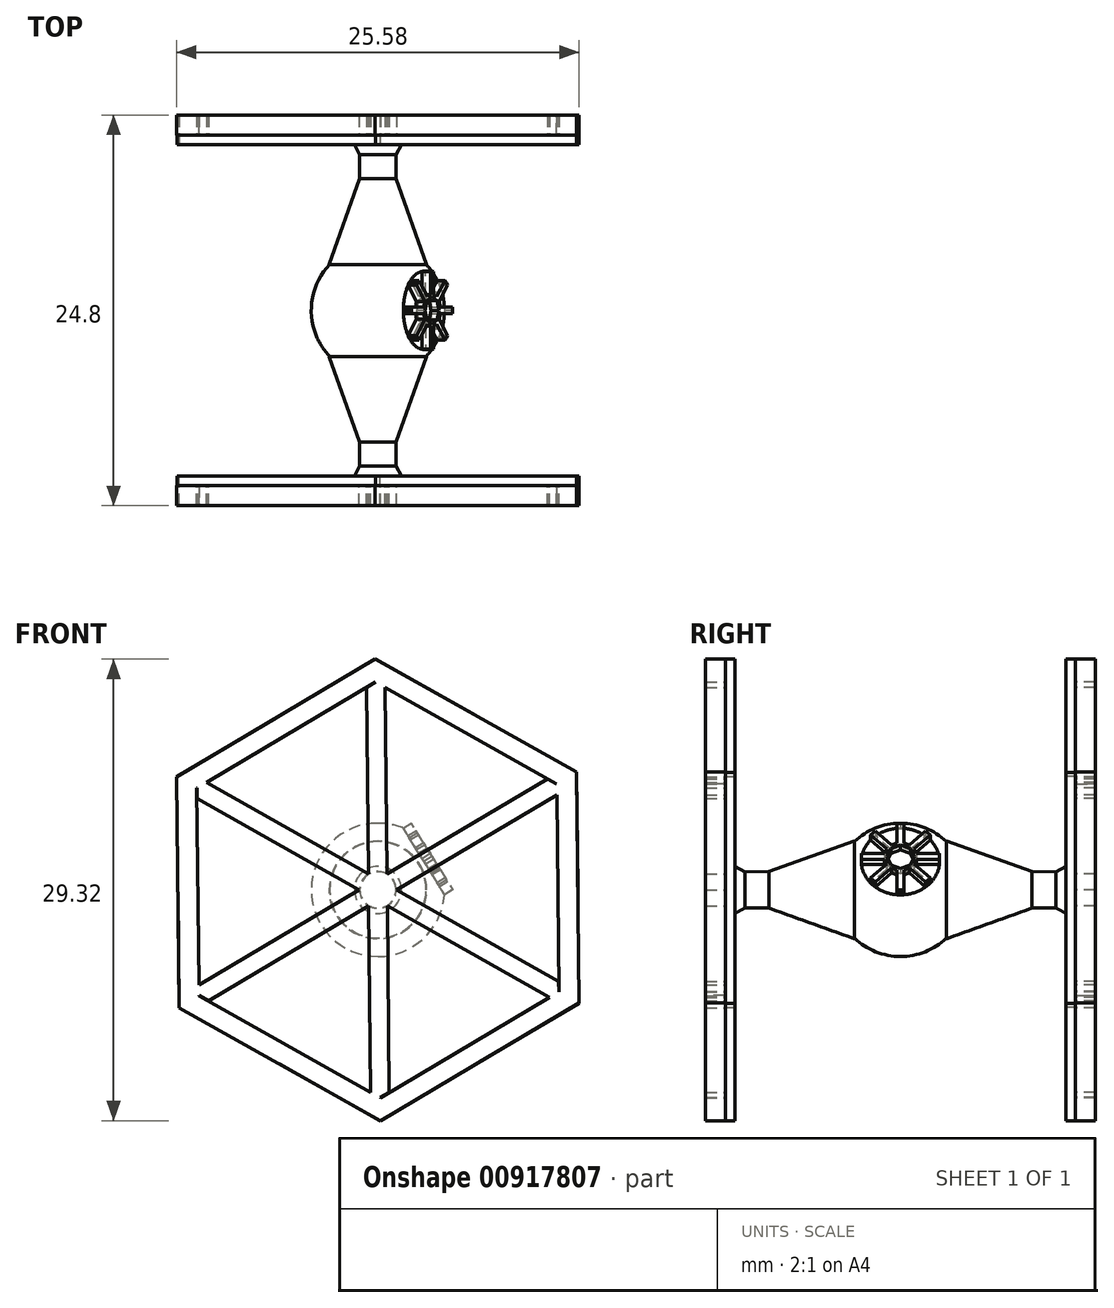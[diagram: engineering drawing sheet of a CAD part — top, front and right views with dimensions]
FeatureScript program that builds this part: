
annotation { "Feature Type Name" : "Feature", "Feature Type Description" : "" }
export const myFeature = defineFeature(function(context is Context, id is Id, definition is map)
    precondition{}
    {
        {
            var Q0;
            Q0=qCreatedBy(makeId("Front.planeOp"),FACE);
            var sketch = newSketch(context, id + "F0", { "sketchPlane" : qUnion([Q0])});
            skArc(sketch, "E0", {"start": v(0, 4.23) * mm, "mid": v(4.23, 0) * mm, "end": v(0, -4.23) * mm});
            skLineSegment(sketch, "E1", {"start": v(0, 4.23) * mm, "end": v(0, -4.23) * mm});
            skSolve(sketch);
        }
        {
            var Q0;
            Q0=qSketchRegion(id+"F0",true);
            var Q1;
            Q1=sQuery(id+"F0.wireOp",EDGE,"E1");
            revolve(context, id + "F1", {"surfaceOperationType" : NewSurfaceOperationType.NEW, "entities" : qUnion([Q0]), "axis" : qUnion([Q1]), "revolveType" : RevolveType.ONE_DIRECTION, "angle" : 180 * degree});
        }
        {
            var Q0;
            Q0=qCreatedBy(makeId("Right.planeOp"),FACE);
            var sketch = newSketch(context, id + "F2", { "sketchPlane" : qUnion([Q0])});
            skLineSegment(sketch, "E2", {"start": v(-10.52, 0) * mm, "end": v(0, 0) * mm});
            skLineSegment(sketch, "E3", {"start": v(-10.52, 0) * mm, "end": v(-10.52, 1.15) * mm});
            skLineSegment(sketch, "E4", {"start": v(-2.92, 3.1) * mm, "end": v(-2.92, 0) * mm});
            skLineSegment(sketch, "E5", {"start": v(-2.92, 0) * mm, "end": v(0, 0) * mm});
            skLineSegment(sketch, "E6", {"start": v(-2.92, 3.1) * mm, "end": v(-8.36, 1.16) * mm});
            skLineSegment(sketch, "E7", {"start": v(-8.36, 1.16) * mm, "end": v(-9.88, 1.15) * mm});
            skLineSegment(sketch, "E8", {"start": v(-9.88, 1.15) * mm, "end": v(-10.52, 1.5) * mm});
            skLineSegment(sketch, "E9", {"start": v(-10.52, 1.5) * mm, "end": v(-10.52, 1.15) * mm});
            skLineSegment(sketch, "E10", {"start": v(-10.52, 1.15) * mm, "end": v(-6.39, 1.17) * mm, "construction": true});
            skSolve(sketch);
        }
        {
            var Q0;
            {var subQ1=sQuery(id+"F2.wireOp",EDGE,"E3");Q0=makeQuery(id+"F2.imprint","IMPRINT",FACE,{"disambiguationData":[TD([[makeQuery(id+"F2.imprint","IMPRINT",EDGE,{"derivedFrom":subQ1}),-1.0]])]});}
            var Q1;
            Q1=sQuery(id+"F2.wireOp",EDGE,"E2");
            revolve(context, id + "F3", {"operationType" : NewBodyOperationType.ADD, "surfaceOperationType" : NewSurfaceOperationType.NEW, "entities" : qUnion([Q0]), "axis" : qUnion([Q1]), "revolveType" : RevolveType.FULL});
        }
        {
            var Q0;
            Q0=qCreatedBy(makeId("Front.planeOp"),FACE);
            var sketch = newSketch(context, id + "F4", { "sketchPlane" : qUnion([Q0])});
            skLineSegment(sketch, "E11", {"start": v(2.92, 1.8) * mm, "end": v(0, 0) * mm});
            skSolve(sketch);
        }
        {
            var Q0;
            Q0=makeQuery(id+"F3.opRevolve","SWEPT_FACE",FACE,{"disambiguationData":[OSD([sQuery(id+"F2.wireOp",EDGE,"E3")])]});
            cPlane(context, id + "F5", {"entities" : qUnion([Q0]), "cplaneType" : CPlaneType.OFFSET, "offset" : 0 * mm, "width" : 152.4 * mm, "height" : 152.4 * mm});
        }
        {
            var Q0;
            Q0=qCreatedBy(id+"F5.planeOp",FACE);
            var sketch = newSketch(context, id + "F6", { "sketchPlane" : qUnion([Q0])});
            skCircle(sketch, "E12.cCircle", {"center": v(0, 0) * mm, "radius": 12.7 * mm, "construction": true});
            skLineSegment(sketch, "E12.0", {"start": v(12.77, -7.21) * mm, "end": v(0.14, -14.66) * mm});
            skLineSegment(sketch, "E12.1", {"start": v(0.14, -14.66) * mm, "end": v(-12.63, -7.45) * mm});
            skLineSegment(sketch, "E12.2", {"start": v(-12.63, -7.45) * mm, "end": v(-12.77, 7.21) * mm});
            skLineSegment(sketch, "E12.3", {"start": v(-12.77, 7.21) * mm, "end": v(-0.14, 14.66) * mm});
            skLineSegment(sketch, "E12.4", {"start": v(-0.14, 14.66) * mm, "end": v(12.63, 7.45) * mm});
            skLineSegment(sketch, "E12.5", {"start": v(12.63, 7.45) * mm, "end": v(12.77, -7.21) * mm});
            skPoint(sketch, "E12.0.midPoint", {"position": v(6.45, -10.94) * mm});
            skSolve(sketch);
        }
        {
            var Q0;
            Q0=qSketchRegion(id+"F6",true);
            extrude(context, id + "F7", {"entities" : qUnion([Q0]), "depth" : 0.6 * mm, "offsetDistance" : 25.4 * mm});
        }
        {
            var Q0;
            Q0=makeQuery(id+"F7.opExtrude","CAP_FACE",FACE,{"disambiguationData":[OSD([sQuery(id+"F6.wireOp",EDGE,"E12.0"),sQuery(id+"F6.wireOp",EDGE,"E12.1"),sQuery(id+"F6.wireOp",EDGE,"E12.2"),sQuery(id+"F6.wireOp",EDGE,"E12.3"),sQuery(id+"F6.wireOp",EDGE,"E12.4"),sQuery(id+"F6.wireOp",EDGE,"E12.5")])],"isStart":false});
            var sketch = newSketch(context, id + "F8", { "sketchPlane" : qUnion([Q0])});
            skCircle(sketch, "E13.cCircle", {"center": v(0, 0) * mm, "radius": 1.02 * mm, "construction": true});
            skLineSegment(sketch, "E13.0", {"start": v(-0.6, 1.02) * mm, "end": v(0.58, 1.03) * mm});
            skLineSegment(sketch, "E13.1", {"start": v(0.58, 1.03) * mm, "end": v(1.18, 0.01) * mm});
            skLineSegment(sketch, "E13.2", {"start": v(1.18, 0.01) * mm, "end": v(0.6, -1.02) * mm});
            skLineSegment(sketch, "E13.3", {"start": v(0.6, -1.02) * mm, "end": v(-0.58, -1.03) * mm});
            skLineSegment(sketch, "E13.4", {"start": v(-0.58, -1.03) * mm, "end": v(-1.18, -0.01) * mm});
            skLineSegment(sketch, "E13.5", {"start": v(-1.18, -0.01) * mm, "end": v(-0.6, 1.02) * mm});
            skPoint(sketch, "E13.0.midPoint", {"position": v(0, 1.02) * mm});
            skLineSegment(sketch, "E14", {"start": v(0.9, -0.5) * mm, "end": v(11.5, -6.49) * mm, "construction": true});
            skLineSegment(sketch, "E15", {"start": v(1.18, 0.01) * mm, "end": v(11.48, -5.8) * mm});
            skLineSegment(sketch, "E16", {"start": v(0.6, -1.02) * mm, "end": v(10.9, -6.83) * mm});
            skLineSegment(sketch, "E17", {"start": v(10.9, -6.83) * mm, "end": v(11.5, -6.49) * mm});
            skLineSegment(sketch, "E18", {"start": v(11.48, -5.8) * mm, "end": v(11.5, -6.49) * mm});
            skLineSegment(sketch, "E19", {"start": v(0.58, 1.03) * mm, "end": v(10.78, 7.05) * mm});
            skLineSegment(sketch, "E20", {"start": v(1.18, 0.01) * mm, "end": v(11.37, 6.03) * mm});
            skLineSegment(sketch, "E21", {"start": v(0.88, 0.52) * mm, "end": v(11.37, 6.71) * mm, "construction": true});
            skLineSegment(sketch, "E22", {"start": v(11.37, 6.71) * mm, "end": v(11.37, 6.03) * mm});
            skLineSegment(sketch, "E23", {"start": v(11.37, 6.71) * mm, "end": v(10.78, 7.05) * mm});
            skLineSegment(sketch, "E24", {"start": v(-0.6, 1.02) * mm, "end": v(-0.72, 12.86) * mm});
            skLineSegment(sketch, "E25", {"start": v(-0.72, 12.86) * mm, "end": v(-0.13, 13.2) * mm});
            skLineSegment(sketch, "E26", {"start": v(0.58, 1.03) * mm, "end": v(0.46, 12.86) * mm});
            skLineSegment(sketch, "E27", {"start": v(0.46, 12.86) * mm, "end": v(-0.13, 13.2) * mm});
            skLineSegment(sketch, "E28", {"start": v(-0.6, 1.02) * mm, "end": v(0.6, -1.02) * mm, "construction": true});
            skLineSegment(sketch, "E29.MirrorCS", {"start": v(-0.58, -1.03) * mm, "end": v(-10.77, -7.04) * mm});
            skLineSegment(sketch, "E30.MirrorCS", {"start": v(-0.88, -0.52) * mm, "end": v(-11.37, -6.71) * mm, "construction": true});
            skLineSegment(sketch, "E31.MirrorCS", {"start": v(-1.18, -0.01) * mm, "end": v(-11.38, -6.03) * mm});
            skLineSegment(sketch, "E32.MirrorCS", {"start": v(-11.37, -6.71) * mm, "end": v(-11.38, -6.03) * mm});
            skLineSegment(sketch, "E33.MirrorCS", {"start": v(-11.37, -6.71) * mm, "end": v(-10.77, -7.04) * mm});
            skLineSegment(sketch, "E34", {"start": v(-1.18, -0.01) * mm, "end": v(1.18, 0.01) * mm, "construction": true});
            skLineSegment(sketch, "E35", {"start": v(-0.58, -1.03) * mm, "end": v(0.58, 1.03) * mm, "construction": true});
            skLineSegment(sketch, "E36.MirrorCS", {"start": v(-0.58, -1.03) * mm, "end": v(-0.46, -12.87) * mm});
            skLineSegment(sketch, "E37.MirrorCS", {"start": v(0.6, -1.02) * mm, "end": v(0.72, -12.85) * mm});
            skLineSegment(sketch, "E38.MirrorCS", {"start": v(-0.46, -12.87) * mm, "end": v(0.13, -13.2) * mm});
            skLineSegment(sketch, "E39.MirrorCS", {"start": v(0.72, -12.85) * mm, "end": v(0.13, -13.2) * mm});
            skLineSegment(sketch, "E40.MirrorCS", {"start": v(-0.6, 1.02) * mm, "end": v(-10.9, 6.83) * mm});
            skLineSegment(sketch, "E41.MirrorCS", {"start": v(-1.18, -0.01) * mm, "end": v(-11.49, 5.8) * mm});
            skLineSegment(sketch, "E42.MirrorCS", {"start": v(-0.9, 0.5) * mm, "end": v(-11.5, 6.49) * mm, "construction": true});
            skLineSegment(sketch, "E43.MirrorCS", {"start": v(-10.9, 6.83) * mm, "end": v(-11.5, 6.49) * mm});
            skLineSegment(sketch, "E44.MirrorCS", {"start": v(-11.49, 5.8) * mm, "end": v(-11.5, 6.49) * mm});
            skSolve(sketch);
        }
        {
            var Q0;
            Q0=qSketchRegion(id+"F8",true);
            extrude(context, id + "F9", {"entities" : qUnion([Q0]), "depth" : 1.27 * mm, "offsetDistance" : 25.4 * mm});
        }
        {
            var Q0;
            Q0=makeQuery(id+"F7.opExtrude","CAP_FACE",FACE,{"disambiguationData":[OSD([sQuery(id+"F6.wireOp",EDGE,"E12.0"),sQuery(id+"F6.wireOp",EDGE,"E12.1"),sQuery(id+"F6.wireOp",EDGE,"E12.2"),sQuery(id+"F6.wireOp",EDGE,"E12.3"),sQuery(id+"F6.wireOp",EDGE,"E12.4"),sQuery(id+"F6.wireOp",EDGE,"E12.5")])],"isStart":false});
            var sketch = newSketch(context, id + "F10", { "sketchPlane" : qUnion([Q0])});
            skCircle(sketch, "E45.cCircle", {"center": v(0, 0) * mm, "radius": 12.7 * mm, "construction": true});
            skLineSegment(sketch, "E45.0", {"start": v(0.17, -14.66) * mm, "end": v(-12.61, -7.48) * mm});
            skLineSegment(sketch, "E45.1", {"start": v(-12.61, -7.48) * mm, "end": v(-12.79, 7.18) * mm});
            skLineSegment(sketch, "E45.2", {"start": v(-12.79, 7.18) * mm, "end": v(-0.17, 14.66) * mm});
            skLineSegment(sketch, "E45.3", {"start": v(-0.17, 14.66) * mm, "end": v(12.61, 7.48) * mm});
            skLineSegment(sketch, "E45.4", {"start": v(12.61, 7.48) * mm, "end": v(12.79, -7.18) * mm});
            skLineSegment(sketch, "E45.5", {"start": v(12.79, -7.18) * mm, "end": v(0.17, -14.66) * mm});
            skPoint(sketch, "E45.0.midPoint", {"position": v(-6.22, -11.07) * mm});
            skCircle(sketch, "E46.cCircle", {"center": v(0, 0) * mm, "radius": 11.43 * mm, "construction": true});
            skLineSegment(sketch, "E46.0", {"start": v(11.5, -6.46) * mm, "end": v(0.16, -13.2) * mm});
            skLineSegment(sketch, "E46.1", {"start": v(0.16, -13.2) * mm, "end": v(-11.35, -6.73) * mm});
            skLineSegment(sketch, "E46.2", {"start": v(-11.35, -6.73) * mm, "end": v(-11.5, 6.46) * mm});
            skLineSegment(sketch, "E46.3", {"start": v(-11.5, 6.46) * mm, "end": v(-0.16, 13.2) * mm});
            skLineSegment(sketch, "E46.4", {"start": v(-0.16, 13.2) * mm, "end": v(11.35, 6.73) * mm});
            skLineSegment(sketch, "E46.5", {"start": v(11.35, 6.73) * mm, "end": v(11.5, -6.46) * mm});
            skPoint(sketch, "E46.0.midPoint", {"position": v(5.83, -9.83) * mm});
            skLineSegment(sketch, "E47", {"start": v(0, 0) * mm, "end": v(-0.16, 13.2) * mm, "construction": true});
            skSolve(sketch);
        }
        {
            var Q0;
            Q0=qSketchRegion(id+"F10",true);
            extrude(context, id + "F11", {"entities" : qUnion([Q0]), "operationType" : NewBodyOperationType.ADD, "depth" : 1.27 * mm, "offsetDistance" : 25.4 * mm});
        }
        {
            var Q0;
            Q0=makeQuery(id+"F1.opRevolve","SWEPT_BODY",BODY,{"disambiguationData":[OSD([sQuery(id+"F0.wireOp",EDGE,"E0"),sQuery(id+"F0.wireOp",EDGE,"E1")])]});
            var Q1;
            Q1=makeQuery(id+"F11.opExtrude","SWEPT_BODY",BODY,{"disambiguationData":[OSD([sQuery(id+"F10.wireOp",EDGE,"E45.0"),sQuery(id+"F10.wireOp",EDGE,"E45.1"),sQuery(id+"F10.wireOp",EDGE,"E45.2"),sQuery(id+"F10.wireOp",EDGE,"E45.3"),sQuery(id+"F10.wireOp",EDGE,"E45.4"),sQuery(id+"F10.wireOp",EDGE,"E45.5"),sQuery(id+"F10.wireOp",EDGE,"E46.0"),sQuery(id+"F10.wireOp",EDGE,"E46.1"),sQuery(id+"F10.wireOp",EDGE,"E46.2"),sQuery(id+"F10.wireOp",EDGE,"E46.3"),sQuery(id+"F10.wireOp",EDGE,"E46.4"),sQuery(id+"F10.wireOp",EDGE,"E46.5")])]});
            var Q2;
            Q2=makeQuery(id+"F9.opExtrude","SWEPT_BODY",BODY,{"disambiguationData":[OSD([sQuery(id+"F8.wireOp",EDGE,"e4088l3h-TRdP-YUV1-DimP-QgpoRXoSz6zW"),sQuery(id+"F8.wireOp",EDGE,"rNqrBlr8-UcBL-GZNG-r5H9-K651OJBnXBdF"),sQuery(id+"F8.wireOp",EDGE,"XT5MB1Ta-hpCc-D5US-sxoT-k3o21iWepZKP"),sQuery(id+"F8.wireOp",EDGE,"ia7Jvukh-ZUJa-dcwM-fXNi-vXRkq6ZTCWAl"),sQuery(id+"F8.wireOp",EDGE,"t7KdV7Ep-AOKE-F29g-YpIB-QDUs5oZ9mr9M")])]});
            var Q3;
            Q3=makeQuery(id+"F7.opExtrude","SWEPT_BODY",BODY,{"disambiguationData":[OSD([sQuery(id+"F6.wireOp",EDGE,"E12.0"),sQuery(id+"F6.wireOp",EDGE,"E12.1"),sQuery(id+"F6.wireOp",EDGE,"E12.2"),sQuery(id+"F6.wireOp",EDGE,"E12.3"),sQuery(id+"F6.wireOp",EDGE,"E12.4"),sQuery(id+"F6.wireOp",EDGE,"E12.5")])]});
            var Q4;
            Q4=makeQuery(id+"F9.opExtrude","SWEPT_BODY",BODY,{"disambiguationData":[OSD([sQuery(id+"F8.wireOp",EDGE,"h5ovLTEs-Qimv-JSNO-7XFy-4wTh3neFp6lt"),sQuery(id+"F8.wireOp",EDGE,"HcRdqBJa-9mo1-5534-Od7W-gK9DLAlOhv5E"),sQuery(id+"F8.wireOp",EDGE,"MGMhxXdO-j8ME-eP1w-4p00-L4sKs11Nsue0"),sQuery(id+"F8.wireOp",EDGE,"5Or9xO9C-o0LV-kDc4-zgoI-hLg2F0xFyjbs"),sQuery(id+"F8.wireOp",EDGE,"yWwAQ9ya-vrHy-8gJy-HAmC-oWqf2xZRePRL")])]});
            var Q5;
            Q5=makeQuery(id+"F9.opExtrude","SWEPT_BODY",BODY,{"disambiguationData":[OSD([sQuery(id+"F8.wireOp",EDGE,"VzNwZegU-slTl-zrlu-WjOM-1HgJ77omgEMa"),sQuery(id+"F8.wireOp",EDGE,"SmjYTKC0-uZeK-tFon-CS8w-A28pdUwgq57T"),sQuery(id+"F8.wireOp",EDGE,"I9094Run-MDG7-CHYL-MPFA-Pd3m6BzciPO7"),sQuery(id+"F8.wireOp",EDGE,"REXvvXLX-WvZ0-wZP4-pBNv-99FpaeRVCB4q"),sQuery(id+"F8.wireOp",EDGE,"eHpNHtED-JKNh-z9jY-fupS-0KnVNc75jVcw")])]});
            var Q6;
            Q6=makeQuery(id+"F9.opExtrude","SWEPT_BODY",BODY,{"disambiguationData":[OSD([sQuery(id+"F8.wireOp",EDGE,"fAG5c1Hs-o2vG-24OK-IYwM-YdrNWbWpHdfn"),sQuery(id+"F8.wireOp",EDGE,"SEygHRAC-42re-gz6e-tUOe-WRzYkIW6SOBE"),sQuery(id+"F8.wireOp",EDGE,"LOzhPPDl-ORCB-veFE-VDiC-yFwJ4bEGiqIK"),sQuery(id+"F8.wireOp",EDGE,"CwswoNC1-oiif-SFKw-JQ9u-itZsdomRdLiL"),sQuery(id+"F8.wireOp",EDGE,"hsp4RkjB-uVeo-Kqf3-IJRF-u61o39UKpDb3")])]});
            var Q7;
            Q7=makeQuery(id+"F9.opExtrude","SWEPT_BODY",BODY,{"disambiguationData":[OSD([sQuery(id+"F8.wireOp",EDGE,"cjiXETq2-uRwu-k2y5-Cs5S-D4pdAVLm720i"),sQuery(id+"F8.wireOp",EDGE,"HNXIGHbu-jXZF-RP1S-v1Rg-7EVPwokZSDDq"),sQuery(id+"F8.wireOp",EDGE,"vp6iQiA1-4pxo-fgGo-wVYc-IVz9eX9mKd5D"),sQuery(id+"F8.wireOp",EDGE,"E28nP3MY-u93m-Kkgy-69hQ-WG9A96Vzkkmc"),sQuery(id+"F8.wireOp",EDGE,"2s3GyVWw-IDRb-EWFZ-BIPj-CZhOZjqZTCAU")])]});
            var Q8;
            Q8=makeQuery(id+"F9.opExtrude","SWEPT_BODY",BODY,{"disambiguationData":[OSD([sQuery(id+"F8.wireOp",EDGE,"Io8fTlQo-mJ3e-YKFb-g5va-THQdWxzBNYC9"),sQuery(id+"F8.wireOp",EDGE,"8EuIDoUu-laRL-Bc2g-ZxHQ-4JCyZOk0z9nl"),sQuery(id+"F8.wireOp",EDGE,"PWKXBglR-aBDj-TpwD-orLW-yh5qCQtlrYAR"),sQuery(id+"F8.wireOp",EDGE,"c17j4OZU-Lcra-mNyx-3PDK-vj4ybKLn7ZAD"),sQuery(id+"F8.wireOp",EDGE,"Jon00HQV-VkZ4-Dtdo-KaOh-oMKkTbijA4NB")])]});
            var Q9;
            Q9=makeQuery(id+"F9.opExtrude","SWEPT_BODY",BODY,{"disambiguationData":[OSD([sQuery(id+"F8.wireOp",EDGE,"E15"),sQuery(id+"F8.wireOp",EDGE,"E16"),sQuery(id+"F8.wireOp",EDGE,"E17"),sQuery(id+"F8.wireOp",EDGE,"E18"),sQuery(id+"F8.wireOp",EDGE,"E19"),sQuery(id+"F8.wireOp",EDGE,"E20"),sQuery(id+"F8.wireOp",EDGE,"E22"),sQuery(id+"F8.wireOp",EDGE,"E23"),sQuery(id+"F8.wireOp",EDGE,"E24"),sQuery(id+"F8.wireOp",EDGE,"E25"),sQuery(id+"F8.wireOp",EDGE,"E26"),sQuery(id+"F8.wireOp",EDGE,"E27"),sQuery(id+"F8.wireOp",EDGE,"E29.MirrorCS"),sQuery(id+"F8.wireOp",EDGE,"E31.MirrorCS"),sQuery(id+"F8.wireOp",EDGE,"E32.MirrorCS"),sQuery(id+"F8.wireOp",EDGE,"E33.MirrorCS"),sQuery(id+"F8.wireOp",EDGE,"E36.MirrorCS"),sQuery(id+"F8.wireOp",EDGE,"E37.MirrorCS"),sQuery(id+"F8.wireOp",EDGE,"E38.MirrorCS"),sQuery(id+"F8.wireOp",EDGE,"E39.MirrorCS"),sQuery(id+"F8.wireOp",EDGE,"E40.MirrorCS"),sQuery(id+"F8.wireOp",EDGE,"E41.MirrorCS"),sQuery(id+"F8.wireOp",EDGE,"E43.MirrorCS"),sQuery(id+"F8.wireOp",EDGE,"E44.MirrorCS")])]});
            var Q10;
            Q10=qCreatedBy(makeId("Front.planeOp"),FACE);
            mirror(context, id + "F12", {"entities" : qUnion([Q0, Q1, Q2, Q3, Q4, Q5, Q6, Q7, Q8, Q9]), "mirrorPlane" : qUnion([Q10])});
        }
        {
            var Q0;
            Q0=sQuery(id+"F4.wireOp",VERTEX,"E11.start");
            var Q1;
            Q1=sQuery(id+"F4.wireOp",EDGE,"E11");
            cPlane(context, id + "F13", {"entities" : qUnion([Q0, Q1]), "cplaneType" : CPlaneType.CURVE_POINT, "offset" : 25.4 * mm, "width" : 152.4 * mm, "height" : 152.4 * mm});
        }
        {
            var Q0;
            Q0=qCreatedBy(id+"F13.planeOp",FACE);
            var sketch = newSketch(context, id + "F14", { "sketchPlane" : qUnion([Q0])});
            skCircle(sketch, "E48", {"center": v(0, 0) * mm, "radius": 6.35 * mm});
            skSolve(sketch);
        }
        {
            var Q0;
            Q0=qSketchRegion(id+"F14",true);
            extrude(context, id + "F15", {"entities" : qUnion([Q0]), "operationType" : NewBodyOperationType.REMOVE, "oppositeDirection" : true, "depth" : 25.4 * mm, "offsetDistance" : 25.4 * mm});
        }
        {
            var Q0;
            Q0=qCreatedBy(id+"F13.planeOp",FACE);
            var sketch = newSketch(context, id + "F16", { "sketchPlane" : qUnion([Q0])});
            skCircle(sketch, "E49.cCircle", {"center": v(0, 0) * mm, "radius": 1.02 * mm, "construction": true});
            skLineSegment(sketch, "E49.0", {"start": v(0, -1.1) * mm, "end": v(-0.78, -0.78) * mm});
            skLineSegment(sketch, "E49.1", {"start": v(-0.78, -0.78) * mm, "end": v(-1.1, 0) * mm});
            skLineSegment(sketch, "E49.2", {"start": v(-1.1, 0) * mm, "end": v(-0.78, 0.78) * mm});
            skLineSegment(sketch, "E49.3", {"start": v(-0.78, 0.78) * mm, "end": v(0, 1.1) * mm});
            skLineSegment(sketch, "E49.4", {"start": v(0, 1.1) * mm, "end": v(0.78, 0.78) * mm});
            skLineSegment(sketch, "E49.5", {"start": v(0.78, 0.78) * mm, "end": v(1.1, 0) * mm});
            skLineSegment(sketch, "E49.6", {"start": v(1.1, 0) * mm, "end": v(0.78, -0.78) * mm});
            skLineSegment(sketch, "E49.7", {"start": v(0.78, -0.78) * mm, "end": v(0, -1.1) * mm});
            skCircle(sketch, "E50.cCircle", {"center": v(0, 0) * mm, "radius": 0.8 * mm, "construction": true});
            skLineSegment(sketch, "E50.0", {"start": v(0.62, -0.62) * mm, "end": v(0, -0.87) * mm});
            skLineSegment(sketch, "E50.1", {"start": v(0, -0.87) * mm, "end": v(-0.62, -0.62) * mm});
            skLineSegment(sketch, "E50.2", {"start": v(-0.62, -0.62) * mm, "end": v(-0.87, 0) * mm});
            skLineSegment(sketch, "E50.3", {"start": v(-0.87, 0) * mm, "end": v(-0.62, 0.62) * mm});
            skLineSegment(sketch, "E50.4", {"start": v(-0.62, 0.62) * mm, "end": v(0, 0.87) * mm});
            skLineSegment(sketch, "E50.5", {"start": v(0, 0.87) * mm, "end": v(0.62, 0.62) * mm});
            skLineSegment(sketch, "E50.6", {"start": v(0.62, 0.62) * mm, "end": v(0.87, 0) * mm});
            skLineSegment(sketch, "E50.7", {"start": v(0.87, 0) * mm, "end": v(0.62, -0.62) * mm});
            skPoint(sketch, "E50.0.midPoint", {"position": v(0.3, -0.75) * mm});
            skLineSegment(sketch, "E51", {"start": v(0, 1.1) * mm, "end": v(0.21, 1.1) * mm, "construction": true});
            skLineSegment(sketch, "E52", {"start": v(0, 1.1) * mm, "end": v(-0.21, 1.1) * mm, "construction": true});
            skLineSegment(sketch, "E53", {"start": v(0.78, 0.78) * mm, "end": v(0, 0) * mm, "construction": true});
            skLineSegment(sketch, "E54", {"start": v(0, 0) * mm, "end": v(0.78, -0.78) * mm, "construction": true});
            skLineSegment(sketch, "E55", {"start": v(0, 0) * mm, "end": v(-0.78, -0.78) * mm, "construction": true});
            skLineSegment(sketch, "E56", {"start": v(0, 0) * mm, "end": v(-0.78, 0.78) * mm, "construction": true});
            skLineSegment(sketch, "E57", {"start": v(0.78, 0.78) * mm, "end": v(0.63, 0.93) * mm, "construction": true});
            skLineSegment(sketch, "E58", {"start": v(0.63, 0.93) * mm, "end": v(0.78, 0.78) * mm, "construction": true});
            skLineSegment(sketch, "E59", {"start": v(0.78, 0.78) * mm, "end": v(0.93, 0.63) * mm, "construction": true});
            skLineSegment(sketch, "E60", {"start": v(1.1, 0) * mm, "end": v(1.1, -0.21) * mm, "construction": true});
            skLineSegment(sketch, "E61", {"start": v(1.1, 0) * mm, "end": v(1.1, 0.21) * mm, "construction": true});
            skLineSegment(sketch, "E62", {"start": v(0.78, -0.78) * mm, "end": v(0.63, -0.93) * mm, "construction": true});
            skLineSegment(sketch, "E63", {"start": v(0.78, -0.78) * mm, "end": v(0.93, -0.63) * mm, "construction": true});
            skLineSegment(sketch, "E64", {"start": v(1.1, 0) * mm, "end": v(-1.1, 0) * mm, "construction": true});
            skLineSegment(sketch, "E65", {"start": v(0, 1.1) * mm, "end": v(0, -1.1) * mm, "construction": true});
            skLineSegment(sketch, "E66.MirrorCS", {"start": v(0, -1.1) * mm, "end": v(0.21, -1.1) * mm, "construction": true});
            skLineSegment(sketch, "E67.MirrorCS", {"start": v(0, -1.1) * mm, "end": v(-0.21, -1.1) * mm, "construction": true});
            skLineSegment(sketch, "E68.MirrorCS", {"start": v(-1.1, 0) * mm, "end": v(-1.1, 0.21) * mm, "construction": true});
            skLineSegment(sketch, "E69.MirrorCS", {"start": v(-1.1, 0) * mm, "end": v(-1.1, -0.21) * mm, "construction": true});
            skLineSegment(sketch, "E70.MirrorCS", {"start": v(-0.78, 0.78) * mm, "end": v(-0.63, 0.93) * mm, "construction": true});
            skLineSegment(sketch, "E71.MirrorCS", {"start": v(-0.78, 0.78) * mm, "end": v(-0.93, 0.63) * mm, "construction": true});
            skLineSegment(sketch, "E72.MirrorCS", {"start": v(-0.78, -0.78) * mm, "end": v(-0.93, -0.63) * mm, "construction": true});
            skLineSegment(sketch, "E73.MirrorCS", {"start": v(-0.78, -0.78) * mm, "end": v(0, -1.1) * mm});
            skLineSegment(sketch, "E74.MirrorCS", {"start": v(-0.78, -0.78) * mm, "end": v(-0.63, -0.93) * mm, "construction": true});
            skLineSegment(sketch, "E75", {"start": v(0.21, 1.1) * mm, "end": v(0.21, 1.01) * mm, "construction": true});
            skLineSegment(sketch, "E76", {"start": v(0.21, 1.01) * mm, "end": v(0.21, 2.47) * mm});
            skLineSegment(sketch, "E77", {"start": v(-0.21, 1.1) * mm, "end": v(-0.21, 1.01) * mm, "construction": true});
            skLineSegment(sketch, "E78", {"start": v(-0.21, 1.01) * mm, "end": v(-0.21, 2.47) * mm});
            skLineSegment(sketch, "E79", {"start": v(-0.21, 2.47) * mm, "end": v(0, 2.49) * mm});
            skLineSegment(sketch, "E80", {"start": v(0, 2.49) * mm, "end": v(0.21, 2.47) * mm});
            skLineSegment(sketch, "E81", {"start": v(-0.63, 0.93) * mm, "end": v(-0.57, 0.87) * mm, "construction": true});
            skLineSegment(sketch, "E82", {"start": v(-0.93, 0.63) * mm, "end": v(-0.87, 0.57) * mm, "construction": true});
            skLineSegment(sketch, "E83", {"start": v(-0.57, 0.87) * mm, "end": v(-1.6, 1.9) * mm});
            skLineSegment(sketch, "E84", {"start": v(-0.87, 0.57) * mm, "end": v(-1.9, 1.6) * mm});
            skLineSegment(sketch, "E85", {"start": v(-1.9, 1.6) * mm, "end": v(-1.76, 1.76) * mm});
            skLineSegment(sketch, "E86", {"start": v(-1.76, 1.76) * mm, "end": v(-1.6, 1.9) * mm});
            skLineSegment(sketch, "E87", {"start": v(-1.1, -0.21) * mm, "end": v(-1.01, -0.21) * mm, "construction": true});
            skLineSegment(sketch, "E88", {"start": v(-1.1, 0.21) * mm, "end": v(-1.01, 0.21) * mm, "construction": true});
            skLineSegment(sketch, "E89", {"start": v(0.93, 0.63) * mm, "end": v(0.87, 0.57) * mm, "construction": true});
            skLineSegment(sketch, "E90", {"start": v(0.63, 0.93) * mm, "end": v(0.57, 0.87) * mm, "construction": true});
            skLineSegment(sketch, "E91", {"start": v(0.57, 0.87) * mm, "end": v(1.6, 1.9) * mm});
            skLineSegment(sketch, "E92", {"start": v(0.87, 0.57) * mm, "end": v(1.9, 1.6) * mm});
            skLineSegment(sketch, "E93", {"start": v(1.9, 1.6) * mm, "end": v(1.76, 1.76) * mm});
            skLineSegment(sketch, "E94", {"start": v(1.76, 1.76) * mm, "end": v(1.6, 1.9) * mm});
            skLineSegment(sketch, "E95", {"start": v(0.78, 0.78) * mm, "end": v(1.76, 1.76) * mm, "construction": true});
            skLineSegment(sketch, "E96", {"start": v(0, 1.1) * mm, "end": v(0, 2.49) * mm, "construction": true});
            skLineSegment(sketch, "E97", {"start": v(-0.78, 0.78) * mm, "end": v(-1.76, 1.76) * mm, "construction": true});
            skLineSegment(sketch, "E98", {"start": v(1.1, 0.21) * mm, "end": v(1.01, 0.21) * mm, "construction": true});
            skLineSegment(sketch, "E99", {"start": v(1.1, -0.21) * mm, "end": v(1.01, -0.21) * mm, "construction": true});
            skLineSegment(sketch, "E100", {"start": v(1.01, 0.21) * mm, "end": v(2.47, 0.21) * mm});
            skLineSegment(sketch, "E101", {"start": v(1.01, -0.21) * mm, "end": v(2.47, -0.21) * mm});
            skLineSegment(sketch, "E102", {"start": v(1.1, 0) * mm, "end": v(2.49, 0) * mm, "construction": true});
            skLineSegment(sketch, "E103", {"start": v(2.47, 0.21) * mm, "end": v(2.49, 0) * mm});
            skLineSegment(sketch, "E104", {"start": v(2.47, -0.21) * mm, "end": v(2.49, 0) * mm});
            skLineSegment(sketch, "E105.MirrorCS", {"start": v(-0.57, -0.87) * mm, "end": v(-1.6, -1.9) * mm});
            skLineSegment(sketch, "E106.MirrorCS", {"start": v(-0.87, -0.57) * mm, "end": v(-1.9, -1.6) * mm});
            skLineSegment(sketch, "E107.MirrorCS", {"start": v(-1.76, -1.76) * mm, "end": v(-1.9, -1.6) * mm});
            skLineSegment(sketch, "E108.MirrorCS", {"start": v(-1.6, -1.9) * mm, "end": v(-1.76, -1.76) * mm});
            skLineSegment(sketch, "E109.MirrorCS", {"start": v(-0.78, -0.78) * mm, "end": v(-1.76, -1.76) * mm, "construction": true});
            skLineSegment(sketch, "E110.MirrorCS", {"start": v(0.21, -1.01) * mm, "end": v(0.21, -2.47) * mm});
            skLineSegment(sketch, "E111.MirrorCS", {"start": v(0, -1.1) * mm, "end": v(0, -2.49) * mm, "construction": true});
            skLineSegment(sketch, "E112.MirrorCS", {"start": v(-0.21, -1.01) * mm, "end": v(-0.21, -2.47) * mm});
            skLineSegment(sketch, "E113.MirrorCS", {"start": v(0, -2.49) * mm, "end": v(0.21, -2.47) * mm});
            skLineSegment(sketch, "E114.MirrorCS", {"start": v(-0.21, -2.47) * mm, "end": v(0, -2.49) * mm});
            skLineSegment(sketch, "E115.MirrorCS", {"start": v(0.57, -0.87) * mm, "end": v(1.6, -1.9) * mm});
            skLineSegment(sketch, "E116.MirrorCS", {"start": v(0.78, -0.78) * mm, "end": v(1.76, -1.76) * mm, "construction": true});
            skLineSegment(sketch, "E117.MirrorCS", {"start": v(0.87, -0.57) * mm, "end": v(1.9, -1.6) * mm});
            skLineSegment(sketch, "E118.MirrorCS", {"start": v(1.76, -1.76) * mm, "end": v(1.9, -1.6) * mm});
            skLineSegment(sketch, "E119.MirrorCS", {"start": v(1.6, -1.9) * mm, "end": v(1.76, -1.76) * mm});
            skLineSegment(sketch, "E120.MirrorCS", {"start": v(-1.01, 0.21) * mm, "end": v(-2.47, 0.21) * mm});
            skLineSegment(sketch, "E121.MirrorCS", {"start": v(-1.1, 0) * mm, "end": v(-2.49, 0) * mm, "construction": true});
            skLineSegment(sketch, "E122.MirrorCS", {"start": v(-1.01, -0.21) * mm, "end": v(-2.47, -0.21) * mm});
            skLineSegment(sketch, "E123.MirrorCS", {"start": v(-2.47, -0.21) * mm, "end": v(-2.49, 0) * mm});
            skLineSegment(sketch, "E124.MirrorCS", {"start": v(-2.47, 0.21) * mm, "end": v(-2.49, 0) * mm});
            skSolve(sketch);
        }
        {
            var Q0;
            Q0=qSketchRegion(id+"F16",true);
            extrude(context, id + "F17", {"entities" : qUnion([Q0]), "operationType" : NewBodyOperationType.ADD, "oppositeDirection" : true, "depth" : 0.6 * mm, "offsetDistance" : 25.4 * mm});
        }
    });
